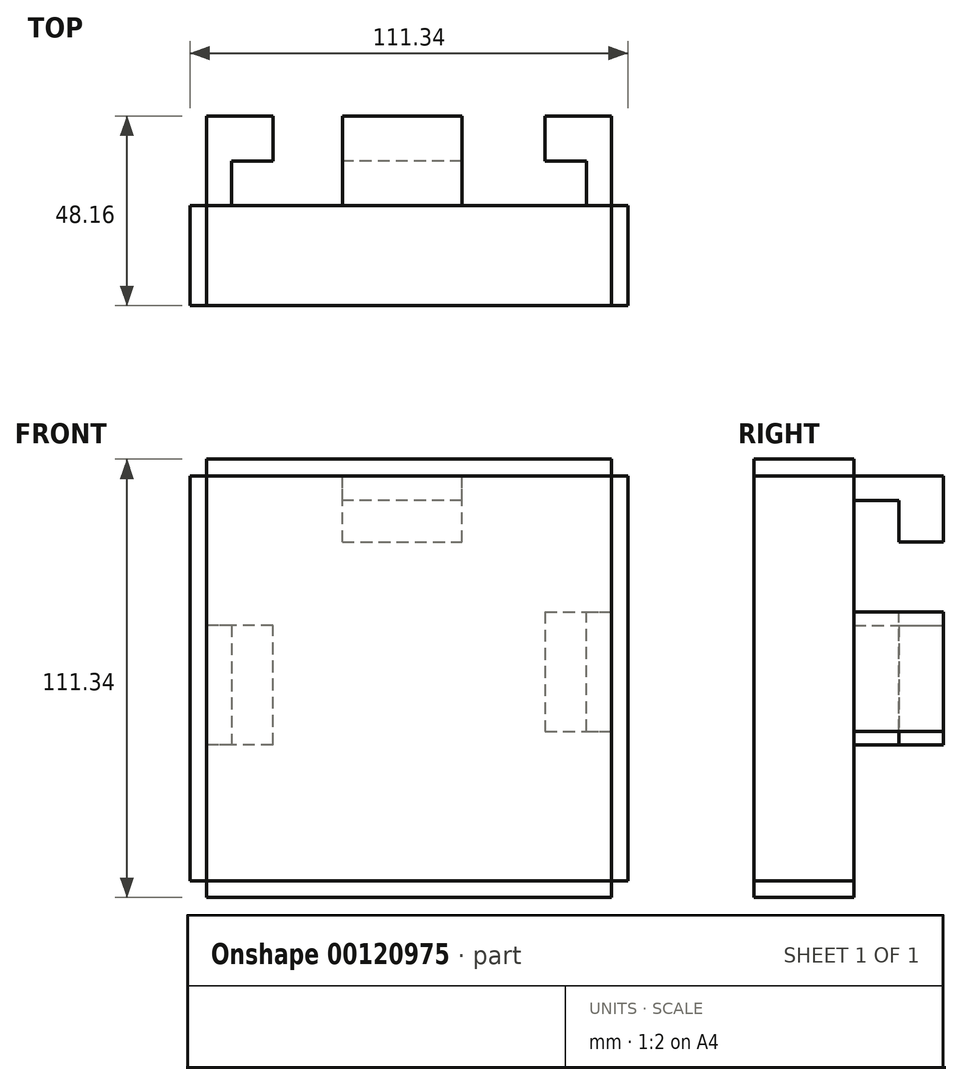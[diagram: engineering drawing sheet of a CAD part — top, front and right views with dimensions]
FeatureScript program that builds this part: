
annotation { "Feature Type Name" : "Feature", "Feature Type Description" : "" }
export const myFeature = defineFeature(function(context is Context, id is Id, definition is map)
    precondition{}
    {
        {
            var Q0;
            Q0=qCreatedBy(makeId("Front.planeOp"),FACE);
            var sketch = newSketch(context, id + "F7", { "sketchPlane" : qUnion([Q0])});
            skLineSegment(sketch, "E0.bottom", {"start": v(51.45, 55.67) * mm, "end": v(-51.45, 55.67) * mm});
            skLineSegment(sketch, "E0.top", {"start": v(51.45, -55.67) * mm, "end": v(-51.45, -55.67) * mm});
            skLineSegment(sketch, "E0.left", {"start": v(51.45, 55.67) * mm, "end": v(51.45, -55.67) * mm});
            skLineSegment(sketch, "E0.right", {"start": v(-51.45, 55.67) * mm, "end": v(-51.45, -55.67) * mm});
            skPoint(sketch, "E0.middle", {"position": v(0, 0) * mm});
            skSolve(sketch);
        }
        {
            var Q0;
            Q0=makeQuery(id+"F7.imprint","IMPRINT",FACE,{"disambiguationData":[TD([[makeQuery(id+"F7.imprint","IMPRINT",EDGE,{"derivedFrom":sQuery(id+"F7.wireOp",EDGE,"E0.bottom")}),1.0]])]});
            extrude(context, id + "F0", {"entities" : qUnion([Q0]), "depth" : 25.4 * mm});
        }
        {
            var Q0;
            Q0=makeQuery(id+"F0.opExtrude","SWEPT_FACE",FACE,{"disambiguationData":[OSD([sQuery(id+"F7.wireOp",EDGE,"E0.right")])]});
            var sketch = newSketch(context, id + "F1", { "sketchPlane" : qUnion([Q0])});
            skLineSegment(sketch, "E1.0", {"start": v(0, 55.67) * mm, "end": v(0, -55.67) * mm});
            skLineSegment(sketch, "E2.bottom", {"start": v(0, -16.9) * mm, "end": v(-22.76, -16.9) * mm});
            skLineSegment(sketch, "E2.top", {"start": v(0, 13.48) * mm, "end": v(-22.76, 13.48) * mm});
            skLineSegment(sketch, "E2.left", {"start": v(0, -16.9) * mm, "end": v(0, 13.48) * mm});
            skLineSegment(sketch, "E2.right", {"start": v(-22.76, -16.9) * mm, "end": v(-22.76, 13.48) * mm});
            skSolve(sketch);
        }
        {
            var Q0;
            Q0=makeQuery(id+"F1.imprint","IMPRINT",FACE,{"disambiguationData":[TD([[makeQuery(id+"F1.imprint","IMPRINT",EDGE,{"derivedFrom":sQuery(id+"F1.wireOp",EDGE,"E2.bottom")}),-1.0]])]});
            extrude(context, id + "F2", {"entities" : qUnion([Q0]), "operationType" : NewBodyOperationType.ADD, "oppositeDirection" : true, "depth" : 6.32 * mm});
        }
        {
            var Q0;
            Q0=makeQuery(id+"F2.opExtrude","CAP_FACE",FACE,{"disambiguationData":[OSD([sQuery(id+"F1.wireOp",EDGE,"E2.bottom"),sQuery(id+"F1.wireOp",EDGE,"E2.top"),sQuery(id+"F1.wireOp",EDGE,"E2.left"),sQuery(id+"F1.wireOp",EDGE,"E2.right")])],"isStart":false});
            var sketch = newSketch(context, id + "F3", { "sketchPlane" : qUnion([Q0])});
            skLineSegment(sketch, "E3.0", {"start": v(22.76, -16.9) * mm, "end": v(22.76, 13.48) * mm});
            skLineSegment(sketch, "E4.bottom", {"start": v(22.76, 13.48) * mm, "end": v(11.38, 13.48) * mm});
            skLineSegment(sketch, "E4.top", {"start": v(22.76, -16.9) * mm, "end": v(11.38, -16.9) * mm});
            skLineSegment(sketch, "E4.left", {"start": v(22.76, 13.48) * mm, "end": v(22.76, -16.9) * mm});
            skLineSegment(sketch, "E4.right", {"start": v(11.38, 13.48) * mm, "end": v(11.38, -16.9) * mm});
            skSolve(sketch);
        }
        {
            var Q0;
            Q0 = qSketchRegion(id + "F3", true);
            extrude(context, id + "F4", {"entities" : qUnion([Q0]), "operationType" : NewBodyOperationType.ADD, "depth" : 10.55 * mm});
        }
        {
            var Q0;
            Q0=qCreatedBy(makeId("Top.planeOp"),FACE);
            var sketch = newSketch(context, id + "F8", { "sketchPlane" : qUnion([Q0])});
            skLineSegment(sketch, "E5", {"start": v(0, 0) * mm, "end": v(0, 175.97) * mm});
            skSolve(sketch);
        }
        {
            var Q0;
            Q0=makeQuery(id+"F0.opExtrude","SWEPT_BODY",BODY,{"disambiguationData":[OSD([sQuery(id+"F7.wireOp",EDGE,"E0.bottom"),sQuery(id+"F7.wireOp",EDGE,"E0.top"),sQuery(id+"F7.wireOp",EDGE,"E0.left"),sQuery(id+"F7.wireOp",EDGE,"E0.right")])]});
            var Q1;
            Q1=sQuery(id+"F8.wireOp",EDGE,"E5");
            circularPattern(context, id + "F5", {"entities" : qUnion([Q0]), "axis" : qUnion([Q1]), "angle" : 90 * degree, "instanceCount" : 3});
        }
    });
